# Revit family: Skylight-Wasco-Barrel_Vault
name_source: partatom
category: Windows
revit_build: Autodesk Revit Architecture 2013 (Build: 20130531_2115(x64)
units: mm (PartAtom-declared; Revit-internal decimal feet)

## types (2) — shared parameters
Arc Height = 0' - 11 19/32"
Arc Width = 3' - 10 1/32"
C Rafter Array = 4
Constraint = 1
Curb = Rubber - Wasco - Black
Curb Height = 0' - 1 1/2"
Curb Width = 0' - 3 1/2"
Default Elevation = 4' - 0"
Description = Glass Glazed Skylights,Continuous Vaulted Systems
Dome Width = 3' - 11 5/8"
Finish = Aluminum - Wasco - Aged Copper
Glass Length = 14' - 11"
Glazing Material = Glass - Wasco - Clear
Height = 1' - 3 21/32"
Length = 15' - 0"
Length Standards = Vertical Ends, 36″ to 123″, Formed Ends, 36″ to 75″
Manufacturer = Wasco Skylights
Model = BV-42
Product Documentation Link = http://www.wascoskylights.com
Product Page URL = http://www.wascoskylights.com
Purlin = No
Rafter Array = 4
Rafter End Offset = 1' - 10 1/2"
Rafter Height = 0' - 11 29/32"
Rafter Width = 3' - 11 5/8"
Rough Height = 1' - 3 21/32"
Rough Length = 15' - 3 5/8"
Rough Width = 4' - 0 5/8"
URL = http://www.wascoskylights.com
V Purlin = No
Width = 3' - 9"
Width Standards = Available in widths of 48″ to 123″ (vertical ends only)

## per-type parameters (varying)
| type | Dome Length | Purlin Constrain | Void Height |
| Formed Ends | 11' - 3" | 1' - 11 5/8" | 0' - 0 1/4" |
| Vertical Ends | 14' - 10" | 0' - 3" | 6' - 0" |

type visibility flags: 2 boolean params named "<type name>" — each type sets only its own to Yes (folded from table)

## geometry (parser evidence)
native form markers: Blend x16, Sweep x22
no freeform markers — native parametric forms only
